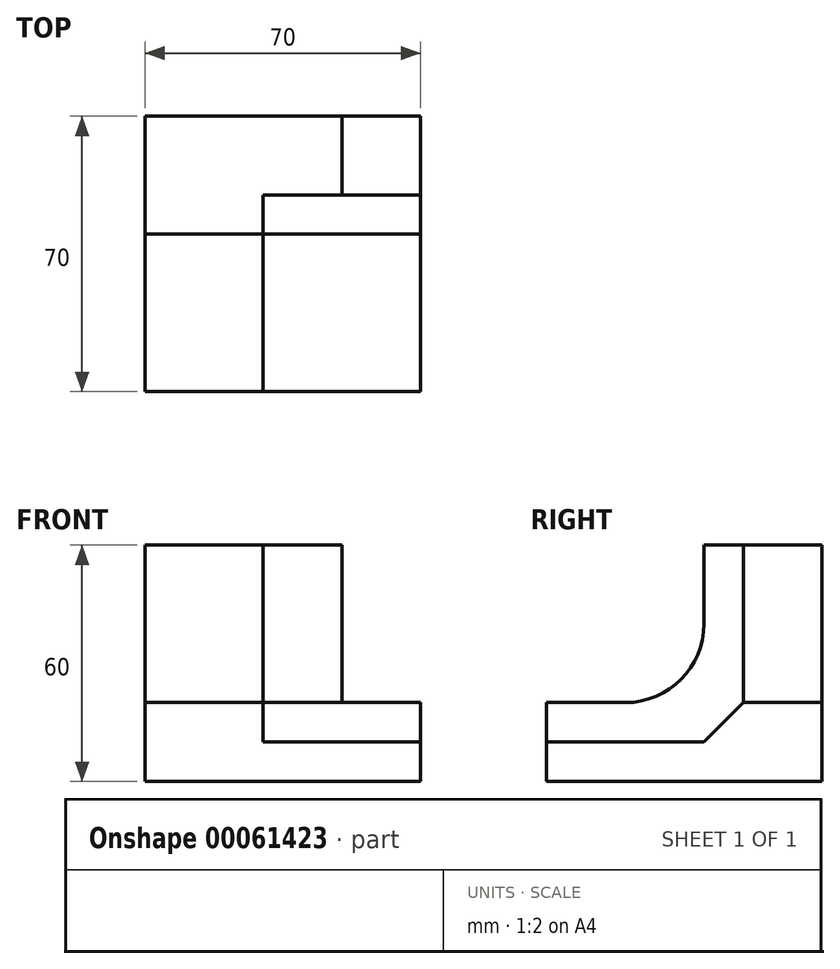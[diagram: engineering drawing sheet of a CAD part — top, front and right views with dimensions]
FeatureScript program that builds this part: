
annotation { "Feature Type Name" : "Feature", "Feature Type Description" : "" }
export const myFeature = defineFeature(function(context is Context, id is Id, definition is map)
    precondition{}
    {
        {
            var Q0;
            Q0=qCreatedBy(makeId("Top.planeOp"),FACE);
            var sketch = newSketch(context, id + "F0", { "sketchPlane" : qUnion([Q0])});
            skLineSegment(sketch, "E0.bottom", {"start": v(0, 0) * mm, "end": v(70, 0) * mm});
            skLineSegment(sketch, "E0.top", {"start": v(0, 70) * mm, "end": v(70, 70) * mm});
            skLineSegment(sketch, "E0.left", {"start": v(0, 0) * mm, "end": v(0, 70) * mm});
            skLineSegment(sketch, "E0.right", {"start": v(70, 0) * mm, "end": v(70, 70) * mm});
            skSolve(sketch);
        }
        {
            var Q0;
            Q0=makeQuery(id+"F0.imprint","IMPRINT",FACE,{"disambiguationData":[TD([[makeQuery(id+"F0.imprint","IMPRINT",EDGE,{"derivedFrom":sQuery(id+"F0.wireOp",EDGE,"E0.bottom")}),1.0]])]});
            extrude(context, id + "F1", {"entities" : qUnion([Q0]), "depth" : 60 * mm});
        }
        {
            var Q0;
            Q0=makeQuery(id+"F1.opExtrude","CAP_FACE",FACE,{"disambiguationData":[OSD([sQuery(id+"F0.wireOp",EDGE,"E0.bottom"),sQuery(id+"F0.wireOp",EDGE,"E0.top"),sQuery(id+"F0.wireOp",EDGE,"E0.left"),sQuery(id+"F0.wireOp",EDGE,"E0.right")])],"isStart":false});
            var sketch = newSketch(context, id + "F2", { "sketchPlane" : qUnion([Q0])});
            skLineSegment(sketch, "E1.bottom", {"start": v(70, 0) * mm, "end": v(30, 0) * mm});
            skLineSegment(sketch, "E1.top", {"start": v(70, 50) * mm, "end": v(30, 50) * mm});
            skLineSegment(sketch, "E1.left", {"start": v(70, 0) * mm, "end": v(70, 50) * mm});
            skLineSegment(sketch, "E1.right", {"start": v(30, 0) * mm, "end": v(30, 50) * mm});
            skSolve(sketch);
        }
        {
            var Q0;
            Q0=makeQuery(id+"F2.imprint","IMPRINT",FACE,{"disambiguationData":[TD([[makeQuery(id+"F2.imprint","IMPRINT",EDGE,{"derivedFrom":sQuery(id+"F2.wireOp",EDGE,"E1.bottom")}),1.0]])]});
            extrude(context, id + "F3", {"entities" : qUnion([Q0]), "operationType" : NewBodyOperationType.REMOVE, "oppositeDirection" : true, "depth" : 50 * mm});
        }
        {
            var Q0;
            Q0=makeQuery(id+"F3.boolean.opBoolean","COPY",FACE,{"derivedFrom":makeQuery(id+"F3.opExtrude","SWEPT_FACE",FACE,{"disambiguationData":[OSD([sQuery(id+"F2.wireOp",EDGE,"E1.top")])]})});
            var sketch = newSketch(context, id + "F4", { "sketchPlane" : qUnion([Q0])});
            skLineSegment(sketch, "E2.bottom", {"start": v(70, 60) * mm, "end": v(50, 60) * mm});
            skLineSegment(sketch, "E2.top", {"start": v(70, 20) * mm, "end": v(50, 20) * mm});
            skLineSegment(sketch, "E2.left", {"start": v(70, 60) * mm, "end": v(70, 20) * mm});
            skLineSegment(sketch, "E2.right", {"start": v(50, 60) * mm, "end": v(50, 20) * mm});
            skSolve(sketch);
        }
        {
            var Q0;
            Q0=makeQuery(id+"F4.imprint","IMPRINT",FACE,{"disambiguationData":[TD([[makeQuery(id+"F4.imprint","IMPRINT",EDGE,{"derivedFrom":sQuery(id+"F4.wireOp",EDGE,"E2.bottom")}),1.0]])]});
            extrude(context, id + "F5", {"entities" : qUnion([Q0]), "operationType" : NewBodyOperationType.REMOVE, "oppositeDirection" : true, "depth" : 20 * mm});
        }
        {
            var Q0;
            Q0=makeQuery(id+"F3.boolean.opBoolean","COPY",FACE,{"derivedFrom":makeQuery(id+"F3.opExtrude","SWEPT_FACE",FACE,{"disambiguationData":[OSD([sQuery(id+"F2.wireOp",EDGE,"E1.right")])]})});
            var sketch = newSketch(context, id + "F6", { "sketchPlane" : qUnion([Q0])});
            skLineSegment(sketch, "E3.bottom", {"start": v(0, 60) * mm, "end": v(40, 60) * mm});
            skLineSegment(sketch, "E3.top", {"start": v(0, 20) * mm, "end": v(40, 20) * mm});
            skLineSegment(sketch, "E3.left", {"start": v(0, 60) * mm, "end": v(0, 20) * mm});
            skLineSegment(sketch, "E3.right", {"start": v(40, 60) * mm, "end": v(40, 20) * mm});
            skSolve(sketch);
        }
        {
            var Q0;
            Q0=makeQuery(id+"F6.imprint","IMPRINT",FACE,{"disambiguationData":[TD([[makeQuery(id+"F6.imprint","IMPRINT",EDGE,{"derivedFrom":sQuery(id+"F6.wireOp",EDGE,"E3.bottom")}),-1.0]])]});
            extrude(context, id + "F7", {"entities" : qUnion([Q0]), "operationType" : NewBodyOperationType.REMOVE, "oppositeDirection" : true, "depth" : 30 * mm});
        }
        {
            var Q0;
            Q0=makeQuery(id+"F7.boolean.opBoolean","COPY",EDGE,{"derivedFrom":makeQuery(id+"F7.opExtrude","SWEPT_EDGE",EDGE,{"disambiguationData":[OSD([sQuery(id+"F6.wireOp",EDGE,"E3.top"),sQuery(id+"F6.wireOp",EDGE,"E3.right")])]})});
            fillet(context, id + "F8", {"entities" : qUnion([Q0]), "radius" : 20 * mm, "tangentPropagation" : true, "allowEdgeOverflow" : false});
        }
        {
            var Q0;
            Q0=makeQuery(id+"F3.boolean.opBoolean","COPY",EDGE,{"derivedFrom":makeQuery(id+"F3.opExtrude","CAP_EDGE",EDGE,{"disambiguationData":[OSD([sQuery(id+"F2.wireOp",EDGE,"E1.top")])],"isStart":false})});
            chamfer(context, id + "F9", {"entities" : qUnion([Q0]), "width" : 10 * mm, "tangentPropagation" : true});
        }
    });
